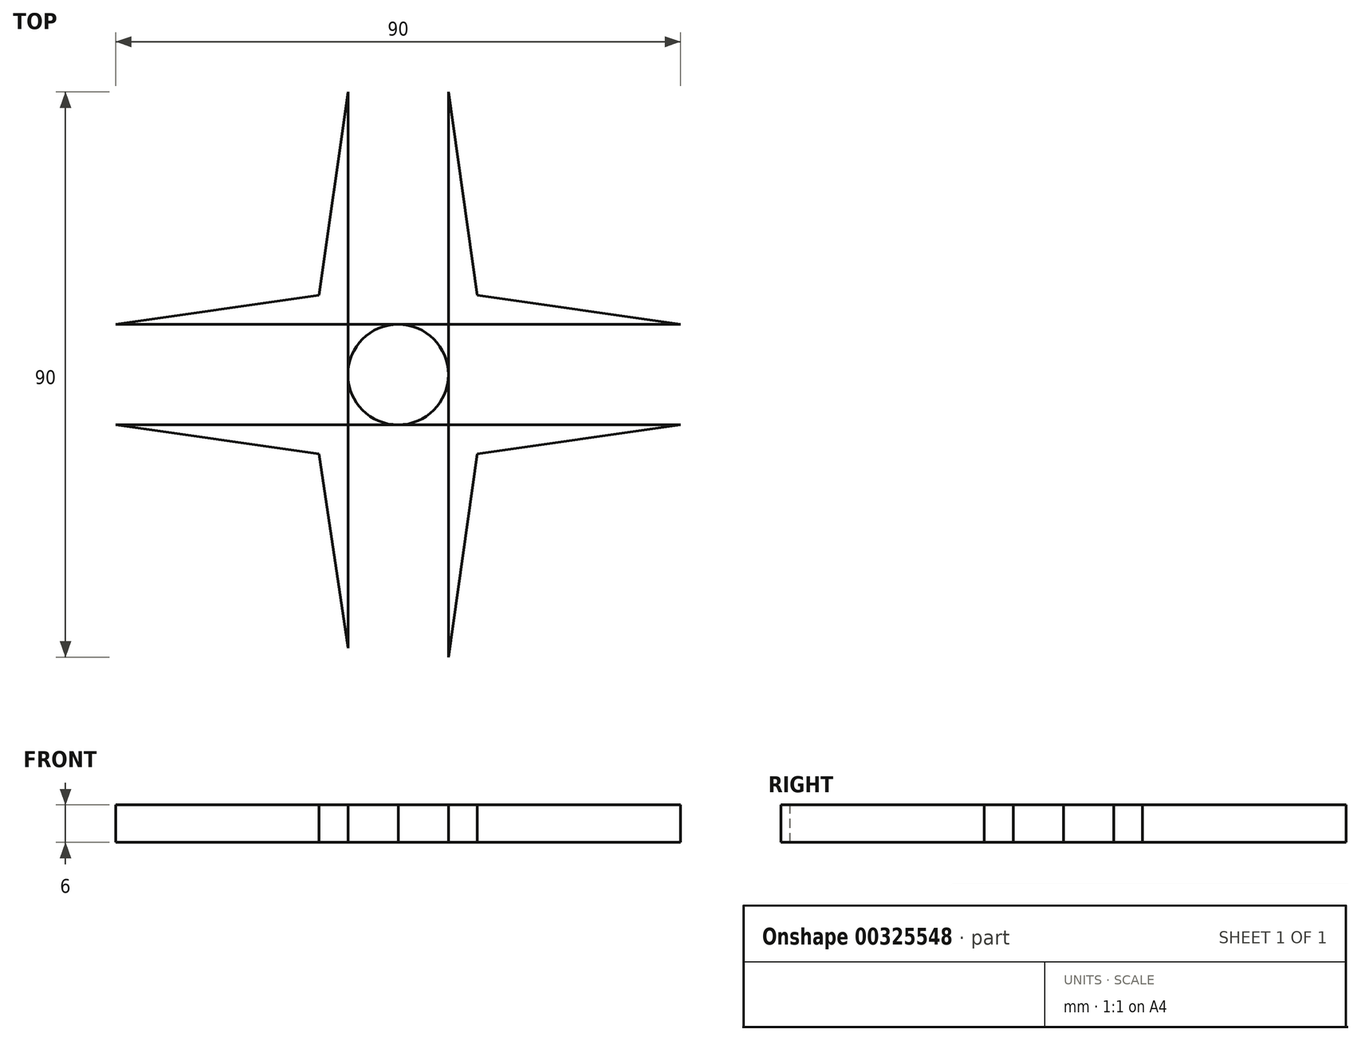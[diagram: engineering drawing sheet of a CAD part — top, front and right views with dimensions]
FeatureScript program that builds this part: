
annotation { "Feature Type Name" : "Feature", "Feature Type Description" : "" }
export const myFeature = defineFeature(function(context is Context, id is Id, definition is map)
    precondition{}
    {
        {
            var Q0;
            Q0=qCreatedBy(makeId("Top.planeOp"),FACE);
            var sketch = newSketch(context, id + "F0", { "sketchPlane" : qUnion([Q0])});
            skLineSegment(sketch, "E0.top", {"start": v(3.66, -2.07) * mm, "end": v(-4.34, -2.07) * mm});
            skLineSegment(sketch, "E1.bottom", {"start": v(-41.34, -2.07) * mm, "end": v(3.66, -2.07) * mm});
            skLineSegment(sketch, "E1.top", {"start": v(-36.34, 5.93) * mm, "end": v(-11.7, 5.93) * mm});
            skLineSegment(sketch, "E1.left", {"start": v(-41.34, -2.07) * mm, "end": v(-41.34, 0.93) * mm});
            skLineSegment(sketch, "E1.right", {"start": v(3.66, -2.07) * mm, "end": v(3.66, 5.93) * mm});
            skLineSegment(sketch, "E2.top", {"start": v(-36.34, -10.07) * mm, "end": v(-13.19, -10.07) * mm});
            skLineSegment(sketch, "E2.left", {"start": v(-41.34, -2.07) * mm, "end": v(-41.34, -5.07) * mm});
            skLineSegment(sketch, "E2.right", {"start": v(3.66, -2.07) * mm, "end": v(3.66, -10.07) * mm});
            skLineSegment(sketch, "E3.bottom", {"start": v(3.66, -47.07) * mm, "end": v(0.66, -47.07) * mm});
            skCircle(sketch, "E4", {"center": v(3.66, -2.07) * mm, "radius": 8 * mm});
            skCircle(sketch, "E5", {"center": v(-18.34, -2.07) * mm, "radius": 2 * mm});
            skCircle(sketch, "E6", {"center": v(-32.34, -2.07) * mm, "radius": 3 * mm});
            skLineSegment(sketch, "E7.1.0", {"start": v(-4.34, -42.07) * mm, "end": v(-4.34, -17.43) * mm});
            skCircle(sketch, "E7.1.1", {"center": v(3.66, -39.07) * mm, "radius": 3 * mm});
            skLineSegment(sketch, "E7.1.2", {"start": v(3.66, -47.07) * mm, "end": v(3.66, -2.07) * mm});
            skCircle(sketch, "E7.1.3", {"center": v(3.66, -24.07) * mm, "radius": 2 * mm});
            skLineSegment(sketch, "E7.1.4", {"start": v(11.66, -42.07) * mm, "end": v(11.66, -18.92) * mm});
            skLineSegment(sketch, "E7.2.0", {"start": v(43.66, -10.07) * mm, "end": v(19.02, -10.07) * mm});
            skCircle(sketch, "E7.2.1", {"center": v(40.66, -2.07) * mm, "radius": 3 * mm});
            skLineSegment(sketch, "E7.2.2", {"start": v(48.66, -2.07) * mm, "end": v(3.66, -2.07) * mm});
            skCircle(sketch, "E7.2.3", {"center": v(25.66, -2.07) * mm, "radius": 2 * mm});
            skLineSegment(sketch, "E7.2.4", {"start": v(43.66, 5.93) * mm, "end": v(20.5, 5.93) * mm});
            skLineSegment(sketch, "E7.3.0", {"start": v(11.66, 37.93) * mm, "end": v(11.66, 13.29) * mm});
            skCircle(sketch, "E7.3.1", {"center": v(3.66, 34.93) * mm, "radius": 3 * mm});
            skLineSegment(sketch, "E7.3.2", {"start": v(3.66, 42.93) * mm, "end": v(3.66, -2.07) * mm});
            skCircle(sketch, "E7.3.3", {"center": v(3.66, 19.93) * mm, "radius": 2 * mm});
            skLineSegment(sketch, "E7.3.4", {"start": v(-4.34, 37.93) * mm, "end": v(-4.34, 14.78) * mm});
            skLineSegment(sketch, "E8", {"start": v(48.66, 0.93) * mm, "end": v(48.66, -5.07) * mm});
            skLineSegment(sketch, "E9", {"start": v(0.66, 42.93) * mm, "end": v(6.66, 42.93) * mm});
            skLineSegment(sketch, "E10", {"start": v(6.66, -47.07) * mm, "end": v(3.66, -47.07) * mm});
            skPoint(sketch, "E11.visualSharp", {"position": v(48.66, 5.93) * mm});
            skPoint(sketch, "E12.visualSharp", {"position": v(48.66, -10.07) * mm});
            skPoint(sketch, "E13.visualSharp", {"position": v(11.66, -47.07) * mm});
            skPoint(sketch, "E14.visualSharp", {"position": v(-4.34, -47.07) * mm});
            skPoint(sketch, "E15.visualSharp", {"position": v(-41.34, 5.93) * mm});
            skPoint(sketch, "E16.visualSharp", {"position": v(-4.34, 42.93) * mm});
            skPoint(sketch, "E17.visualSharp", {"position": v(11.66, 42.93) * mm});
            skLineSegment(sketch, "E18", {"start": v(3.66, 34.93) * mm, "end": v(6.66, 34.93) * mm});
            skLineSegment(sketch, "E19", {"start": v(3.66, 19.93) * mm, "end": v(5.66, 19.93) * mm});
            skLineSegment(sketch, "E20", {"start": v(25.66, -2.07) * mm, "end": v(25.66, -0.07) * mm});
            skLineSegment(sketch, "E21", {"start": v(40.66, -2.07) * mm, "end": v(40.66, 0.93) * mm});
            skLineSegment(sketch, "E22", {"start": v(3.66, -24.07) * mm, "end": v(5.66, -24.07) * mm});
            skLineSegment(sketch, "E23", {"start": v(3.66, -39.07) * mm, "end": v(6.66, -39.07) * mm});
            skLineSegment(sketch, "E24", {"start": v(-18.34, -2.07) * mm, "end": v(-18.34, -4.07) * mm});
            skLineSegment(sketch, "E25", {"start": v(-32.34, -2.07) * mm, "end": v(-32.34, 0.93) * mm});
            skLineSegment(sketch, "E26.bottom", {"start": v(-4.34, -47.07) * mm, "end": v(11.66, -47.07) * mm});
            skLineSegment(sketch, "E26.top", {"start": v(-4.34, 42.93) * mm, "end": v(11.66, 42.93) * mm});
            skLineSegment(sketch, "E26.left", {"start": v(-4.34, -47.07) * mm, "end": v(-4.34, 42.93) * mm});
            skLineSegment(sketch, "E26.right", {"start": v(11.66, -47.07) * mm, "end": v(11.66, 42.93) * mm});
            skLineSegment(sketch, "E27.bottom", {"start": v(-41.34, 5.93) * mm, "end": v(48.66, 5.93) * mm});
            skLineSegment(sketch, "E27.top", {"start": v(-41.34, -10.07) * mm, "end": v(48.66, -10.07) * mm});
            skLineSegment(sketch, "E27.left", {"start": v(-41.34, 5.93) * mm, "end": v(-41.34, -10.07) * mm});
            skLineSegment(sketch, "E27.right", {"start": v(48.66, 5.93) * mm, "end": v(48.66, -10.07) * mm});
            skPoint(sketch, "E28", {"position": v(11.66, -19.3) * mm});
            skPoint(sketch, "E29", {"position": v(20.9, -10.07) * mm});
            skPoint(sketch, "E30", {"position": v(-4.34, -19.3) * mm});
            skPoint(sketch, "E31", {"position": v(-13.57, -10.07) * mm});
            skPoint(sketch, "E32", {"position": v(20.9, 5.93) * mm});
            skPoint(sketch, "E33", {"position": v(11.66, 15.16) * mm});
            skPoint(sketch, "E34", {"position": v(-4.34, 15.16) * mm});
            skPoint(sketch, "E35", {"position": v(-13.57, 5.93) * mm});
            skLineSegment(sketch, "E36", {"start": v(-13.57, 5.93) * mm, "end": v(-4.34, 15.16) * mm});
            skLineSegment(sketch, "E37", {"start": v(11.66, 15.16) * mm, "end": v(20.9, 5.93) * mm});
            skLineSegment(sketch, "E38", {"start": v(20.9, -10.07) * mm, "end": v(11.66, -19.3) * mm});
            skLineSegment(sketch, "E39", {"start": v(-4.34, -19.3) * mm, "end": v(-13.57, -10.07) * mm});
            skLineSegment(sketch, "E40", {"start": v(16.28, -14.69) * mm, "end": v(11.66, -47.07) * mm});
            skLineSegment(sketch, "E41", {"start": v(16.28, -14.69) * mm, "end": v(48.66, -10.07) * mm});
            skLineSegment(sketch, "E42", {"start": v(48.66, 5.93) * mm, "end": v(16.28, 10.55) * mm});
            skLineSegment(sketch, "E43", {"start": v(11.66, 42.93) * mm, "end": v(16.28, 10.55) * mm});
            skLineSegment(sketch, "E44", {"start": v(-4.34, 42.93) * mm, "end": v(-8.96, 10.55) * mm});
            skLineSegment(sketch, "E45", {"start": v(-41.34, 5.93) * mm, "end": v(-8.96, 10.55) * mm});
            skLineSegment(sketch, "E46", {"start": v(-41.34, -10.07) * mm, "end": v(-8.96, -14.69) * mm});
            skLineSegment(sketch, "E47", {"start": v(-8.96, -14.69) * mm, "end": v(-4.34, -45.62) * mm});
            skSolve(sketch);
        }
        {
            var Q0;
            {var subQ0=sQuery(id+"F0.wireOp",EDGE,"E27.top");var subQ1=makeQuery(id+"F0.imprint","IMPRINT",VERTEX,{"disambiguationData":[OD(0.0)],"derivedFrom":subQ0});Q0=makeQuery(id+"F0.imprint","IMPRINT",FACE,{"disambiguationData":[TD([[makeQuery(id+"F0.imprint","IMPRINT",EDGE,{"disambiguationData":[TD([[subQ1,1.0]])],"derivedFrom":subQ0}),1.0]])]});}
            var Q1;
            {var subQ0=sQuery(id+"F0.wireOp",EDGE,"E27.bottom");var subQ1=makeQuery(id+"F0.imprint","IMPRINT",VERTEX,{"disambiguationData":[OD(0.0)],"derivedFrom":subQ0});Q1=makeQuery(id+"F0.imprint","IMPRINT",FACE,{"disambiguationData":[TD([[makeQuery(id+"F0.imprint","IMPRINT",EDGE,{"disambiguationData":[TD([[subQ1,1.0]])],"derivedFrom":subQ0}),-1.0]])]});}
            var Q2;
            {var subQ4=sQuery(id+"F0.wireOp",EDGE,"E36");Q2=makeQuery(id+"F0.imprint","IMPRINT",FACE,{"disambiguationData":[TD([[makeQuery(id+"F0.imprint","IMPRINT",EDGE,{"derivedFrom":subQ4}),-1.0]])]});}
            var Q3;
            {var subQ5=sQuery(id+"F0.wireOp",EDGE,"E26.left");var subQ6=makeQuery(id+"F0.imprint","IMPRINT",VERTEX,{"disambiguationData":[OD(1.0)],"derivedFrom":subQ5});Q3=makeQuery(id+"F0.imprint","IMPRINT",FACE,{"disambiguationData":[TD([[makeQuery(id+"F0.imprint","IMPRINT",EDGE,{"disambiguationData":[TD([[subQ6,1.0]])],"derivedFrom":subQ5}),-1.0]])]});}
            var Q4;
            {var subQ0=sQuery(id+"F0.wireOp",EDGE,"E26.right");var subQ2=makeQuery(id+"F0.imprint","IMPRINT",VERTEX,{"disambiguationData":[OD(1.0)],"derivedFrom":subQ0});Q4=makeQuery(id+"F0.imprint","IMPRINT",FACE,{"disambiguationData":[TD([[makeQuery(id+"F0.imprint","IMPRINT",EDGE,{"disambiguationData":[TD([[subQ2,1.0]])],"derivedFrom":subQ0}),1.0]])]});}
            var Q5;
            {var subQ0=sQuery(id+"F0.wireOp",EDGE,"E37");Q5=makeQuery(id+"F0.imprint","IMPRINT",FACE,{"disambiguationData":[TD([[makeQuery(id+"F0.imprint","IMPRINT",EDGE,{"derivedFrom":subQ0}),-1.0]])]});}
            var Q6;
            {var subQ0=sQuery(id+"F0.wireOp",EDGE,"E27.bottom");var subQ2=makeQuery(id+"F0.imprint","IMPRINT",VERTEX,{"disambiguationData":[OD(1.0)],"derivedFrom":subQ0});Q6=makeQuery(id+"F0.imprint","IMPRINT",FACE,{"disambiguationData":[TD([[makeQuery(id+"F0.imprint","IMPRINT",EDGE,{"disambiguationData":[TD([[subQ2,1.0]])],"derivedFrom":subQ0}),-1.0]])]});}
            var Q7;
            {var subQ7=sQuery(id+"F0.wireOp",EDGE,"E27.top");var subQ13=makeQuery(id+"F0.imprint","IMPRINT",VERTEX,{"disambiguationData":[OD(1.0)],"derivedFrom":subQ7});Q7=makeQuery(id+"F0.imprint","IMPRINT",FACE,{"disambiguationData":[TD([[makeQuery(id+"F0.imprint","IMPRINT",EDGE,{"disambiguationData":[TD([[subQ13,1.0]])],"derivedFrom":subQ7}),1.0]])]});}
            var Q8;
            {var subQ0=sQuery(id+"F0.wireOp",EDGE,"E38");Q8=makeQuery(id+"F0.imprint","IMPRINT",FACE,{"disambiguationData":[TD([[makeQuery(id+"F0.imprint","IMPRINT",EDGE,{"derivedFrom":subQ0}),-1.0]])]});}
            var Q9;
            {var subQ0=sQuery(id+"F0.wireOp",EDGE,"E26.right");var subQ2=makeQuery(id+"F0.imprint","IMPRINT",VERTEX,{"disambiguationData":[OD(0.0)],"derivedFrom":subQ0});Q9=makeQuery(id+"F0.imprint","IMPRINT",FACE,{"disambiguationData":[TD([[makeQuery(id+"F0.imprint","IMPRINT",EDGE,{"disambiguationData":[TD([[subQ2,1.0]])],"derivedFrom":subQ0}),1.0]])]});}
            var Q10;
            {var subQ10=sQuery(id+"F0.wireOp",EDGE,"E26.left");var subQ14=makeQuery(id+"F0.imprint","IMPRINT",VERTEX,{"disambiguationData":[OD(0.0)],"derivedFrom":subQ10});Q10=makeQuery(id+"F0.imprint","IMPRINT",FACE,{"disambiguationData":[TD([[makeQuery(id+"F0.imprint","IMPRINT",EDGE,{"disambiguationData":[TD([[subQ14,1.0]])],"derivedFrom":subQ10}),-1.0]])]});}
            var Q11;
            {var subQ0=sQuery(id+"F0.wireOp",EDGE,"E39");Q11=makeQuery(id+"F0.imprint","IMPRINT",FACE,{"disambiguationData":[TD([[makeQuery(id+"F0.imprint","IMPRINT",EDGE,{"derivedFrom":subQ0}),-1.0]])]});}
            var Q12;
            {var subQ0=sQuery(id+"F0.wireOp",EDGE,"E26.left");var subQ3=sQuery(id+"F0.wireOp",EDGE,"E27.top");var subQ5=makeQuery(id+"F0.imprint","INTERSECT",VERTEX,{"derivedFrom":[subQ0,subQ3]});Q12=makeQuery(id+"F0.imprint","IMPRINT",FACE,{"disambiguationData":[TD([[makeQuery(id+"F0.imprint","IMPRINT",EDGE,{"disambiguationData":[TD([[subQ5,-1.0]])],"derivedFrom":subQ0}),-1.0]])]});}
            var Q13;
            {var subQ0=sQuery(id+"F0.wireOp",EDGE,"E26.right");var subQ3=sQuery(id+"F0.wireOp",EDGE,"E27.top");var subQ5=makeQuery(id+"F0.imprint","INTERSECT",VERTEX,{"derivedFrom":[subQ0,subQ3]});Q13=makeQuery(id+"F0.imprint","IMPRINT",FACE,{"disambiguationData":[TD([[makeQuery(id+"F0.imprint","IMPRINT",EDGE,{"disambiguationData":[TD([[subQ5,-1.0]])],"derivedFrom":subQ0}),1.0]])]});}
            var Q14;
            {var subQ0=sQuery(id+"F0.wireOp",EDGE,"E27.bottom");var subQ3=sQuery(id+"F0.wireOp",EDGE,"E26.right");var subQ5=makeQuery(id+"F0.imprint","INTERSECT",VERTEX,{"derivedFrom":[subQ3,subQ0]});Q14=makeQuery(id+"F0.imprint","IMPRINT",FACE,{"disambiguationData":[TD([[makeQuery(id+"F0.imprint","IMPRINT",EDGE,{"disambiguationData":[TD([[subQ5,1.0]])],"derivedFrom":subQ3}),1.0]])]});}
            var Q15;
            {var subQ0=sQuery(id+"F0.wireOp",EDGE,"E26.left");var subQ3=sQuery(id+"F0.wireOp",EDGE,"E27.bottom");var subQ5=makeQuery(id+"F0.imprint","INTERSECT",VERTEX,{"derivedFrom":[subQ0,subQ3]});Q15=makeQuery(id+"F0.imprint","IMPRINT",FACE,{"disambiguationData":[TD([[makeQuery(id+"F0.imprint","IMPRINT",EDGE,{"disambiguationData":[TD([[subQ5,1.0]])],"derivedFrom":subQ0}),-1.0]])]});}
            var Q16;
            {var subQ0=sQuery(id+"F0.wireOp",EDGE,"E40");Q16=makeQuery(id+"F0.imprint","IMPRINT",FACE,{"disambiguationData":[TD([[makeQuery(id+"F0.imprint","IMPRINT",EDGE,{"derivedFrom":subQ0}),-1.0]])]});}
            var Q17;
            {var subQ4=sQuery(id+"F0.wireOp",EDGE,"E41");Q17=makeQuery(id+"F0.imprint","IMPRINT",FACE,{"disambiguationData":[TD([[makeQuery(id+"F0.imprint","IMPRINT",EDGE,{"derivedFrom":subQ4}),1.0]])]});}
            var Q18;
            {var subQ0=sQuery(id+"F0.wireOp",EDGE,"E27.top");var subQ3=makeQuery(id+"F0.imprint","IMPRINT",VERTEX,{"disambiguationData":[OD(2.0)],"derivedFrom":subQ0});Q18=makeQuery(id+"F0.imprint","IMPRINT",FACE,{"disambiguationData":[TD([[makeQuery(id+"F0.imprint","IMPRINT",EDGE,{"disambiguationData":[TD([[subQ3,1.0]])],"derivedFrom":subQ0}),1.0]])]});}
            var Q19;
            {var subQ5=sQuery(id+"F0.wireOp",EDGE,"E27.bottom");var subQ6=makeQuery(id+"F0.imprint","IMPRINT",VERTEX,{"disambiguationData":[OD(2.0)],"derivedFrom":subQ5});Q19=makeQuery(id+"F0.imprint","IMPRINT",FACE,{"disambiguationData":[TD([[makeQuery(id+"F0.imprint","IMPRINT",EDGE,{"disambiguationData":[TD([[subQ6,1.0]])],"derivedFrom":subQ5}),-1.0]])]});}
            var Q20;
            {var subQ4=sQuery(id+"F0.wireOp",EDGE,"E42");Q20=makeQuery(id+"F0.imprint","IMPRINT",FACE,{"disambiguationData":[TD([[makeQuery(id+"F0.imprint","IMPRINT",EDGE,{"derivedFrom":subQ4}),1.0]])]});}
            var Q21;
            {var subQ4=sQuery(id+"F0.wireOp",EDGE,"E43");Q21=makeQuery(id+"F0.imprint","IMPRINT",FACE,{"disambiguationData":[TD([[makeQuery(id+"F0.imprint","IMPRINT",EDGE,{"derivedFrom":subQ4}),-1.0]])]});}
            var Q22;
            {var subQ0=sQuery(id+"F0.wireOp",EDGE,"E26.right");var subQ1=makeQuery(id+"F0.imprint","IMPRINT",VERTEX,{"disambiguationData":[OD(2.0)],"derivedFrom":subQ0});Q22=makeQuery(id+"F0.imprint","IMPRINT",FACE,{"disambiguationData":[TD([[makeQuery(id+"F0.imprint","IMPRINT",EDGE,{"disambiguationData":[TD([[subQ1,1.0]])],"derivedFrom":subQ0}),1.0]])]});}
            var Q23;
            {var subQ0=sQuery(id+"F0.wireOp",EDGE,"E26.left");var subQ2=makeQuery(id+"F0.imprint","IMPRINT",VERTEX,{"disambiguationData":[OD(2.0)],"derivedFrom":subQ0});Q23=makeQuery(id+"F0.imprint","IMPRINT",FACE,{"disambiguationData":[TD([[makeQuery(id+"F0.imprint","IMPRINT",EDGE,{"disambiguationData":[TD([[subQ2,1.0]])],"derivedFrom":subQ0}),-1.0]])]});}
            var Q24;
            {var subQ4=sQuery(id+"F0.wireOp",EDGE,"E44");Q24=makeQuery(id+"F0.imprint","IMPRINT",FACE,{"disambiguationData":[TD([[makeQuery(id+"F0.imprint","IMPRINT",EDGE,{"derivedFrom":subQ4}),1.0]])]});}
            var Q25;
            {var subQ0=sQuery(id+"F0.wireOp",EDGE,"E45");Q25=makeQuery(id+"F0.imprint","IMPRINT",FACE,{"disambiguationData":[TD([[makeQuery(id+"F0.imprint","IMPRINT",EDGE,{"derivedFrom":subQ0}),-1.0]])]});}
            var Q26;
            {var subQ0=sQuery(id+"F0.wireOp",EDGE,"E46");Q26=makeQuery(id+"F0.imprint","IMPRINT",FACE,{"disambiguationData":[TD([[makeQuery(id+"F0.imprint","IMPRINT",EDGE,{"derivedFrom":subQ0}),1.0]])]});}
            var Q27;
            {var subQ0=sQuery(id+"F0.wireOp",EDGE,"E47");Q27=makeQuery(id+"F0.imprint","IMPRINT",FACE,{"disambiguationData":[TD([[makeQuery(id+"F0.imprint","IMPRINT",EDGE,{"derivedFrom":subQ0}),1.0]])]});}
            extrude(context, id + "F1", {"entities" : qUnion([Q0, Q1, Q2, Q3, Q4, Q5, Q6, Q7, Q8, Q9, Q10, Q11, Q12, Q13, Q14, Q15, Q16, Q17, Q18, Q19, Q20, Q21, Q22, Q23, Q24, Q25, Q26, Q27]), "oppositeDirection" : true, "depth" : 6 * mm});
        }
    });
